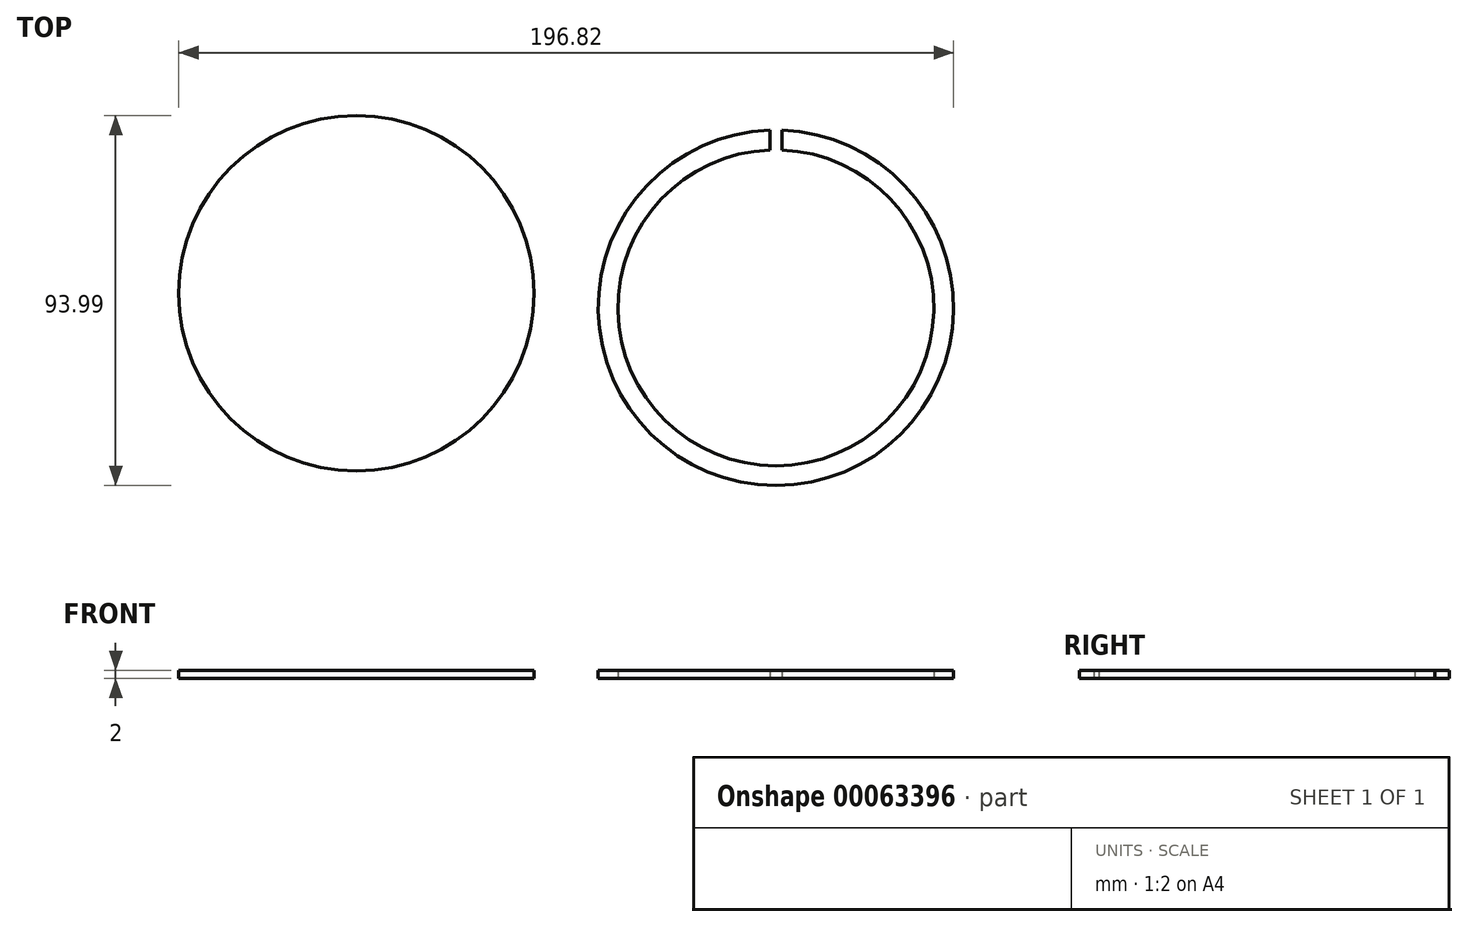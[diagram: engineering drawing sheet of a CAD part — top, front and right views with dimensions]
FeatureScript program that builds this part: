
annotation { "Feature Type Name" : "Feature", "Feature Type Description" : "" }
export const myFeature = defineFeature(function(context is Context, id is Id, definition is map)
    precondition{}
    {
        {
            var Q0;
            Q0=qCreatedBy(makeId("Top.planeOp"),FACE);
            var sketch = newSketch(context, id + "F0", { "sketchPlane" : qUnion([Q0])});
            skCircle(sketch, "E0", {"center": v(-23.5, 18.09) * mm, "radius": 45.13 * mm});
            skSolve(sketch);
        }
        {
            var Q0;
            Q0=qCreatedBy(makeId("Top.planeOp"),FACE);
            var sketch = newSketch(context, id + "F1", { "sketchPlane" : qUnion([Q0])});
            skCircle(sketch, "E1", {"center": v(83.06, 14.37) * mm, "radius": 45.13 * mm});
            skCircle(sketch, "E2", {"center": v(83.06, 14.37) * mm, "radius": 40.14 * mm});
            skLineSegment(sketch, "E3", {"start": v(83.06, 59.5) * mm, "end": v(83.06, 14.37) * mm, "construction": true});
            skLineSegment(sketch, "E4", {"start": v(81.56, 59.48) * mm, "end": v(81.56, 54.48) * mm});
            skLineSegment(sketch, "E5.MirrorCS", {"start": v(84.56, 59.48) * mm, "end": v(84.56, 54.48) * mm});
            skSolve(sketch);
        }
        {
            var Q0;
            Q0=makeQuery(id+"F0.imprint","IMPRINT",FACE,{"disambiguationData":[TD([[makeQuery(id+"F0.imprint","IMPRINT",EDGE,{"derivedFrom":sQuery(id+"F0.wireOp",EDGE,"E0")}),1.0]])]});
            extrude(context, id + "F2", {"entities" : qUnion([Q0]), "depth" : 2 * mm});
        }
        {
            var Q0;
            {var subQ0=sQuery(id+"F1.wireOp",EDGE,"E4");Q0=makeQuery(id+"F1.imprint","IMPRINT",FACE,{"disambiguationData":[TD([[makeQuery(id+"F1.imprint","IMPRINT",EDGE,{"derivedFrom":subQ0}),-1.0]])]});}
            extrude(context, id + "F3", {"entities" : qUnion([Q0]), "depth" : 2 * mm});
        }
    });
